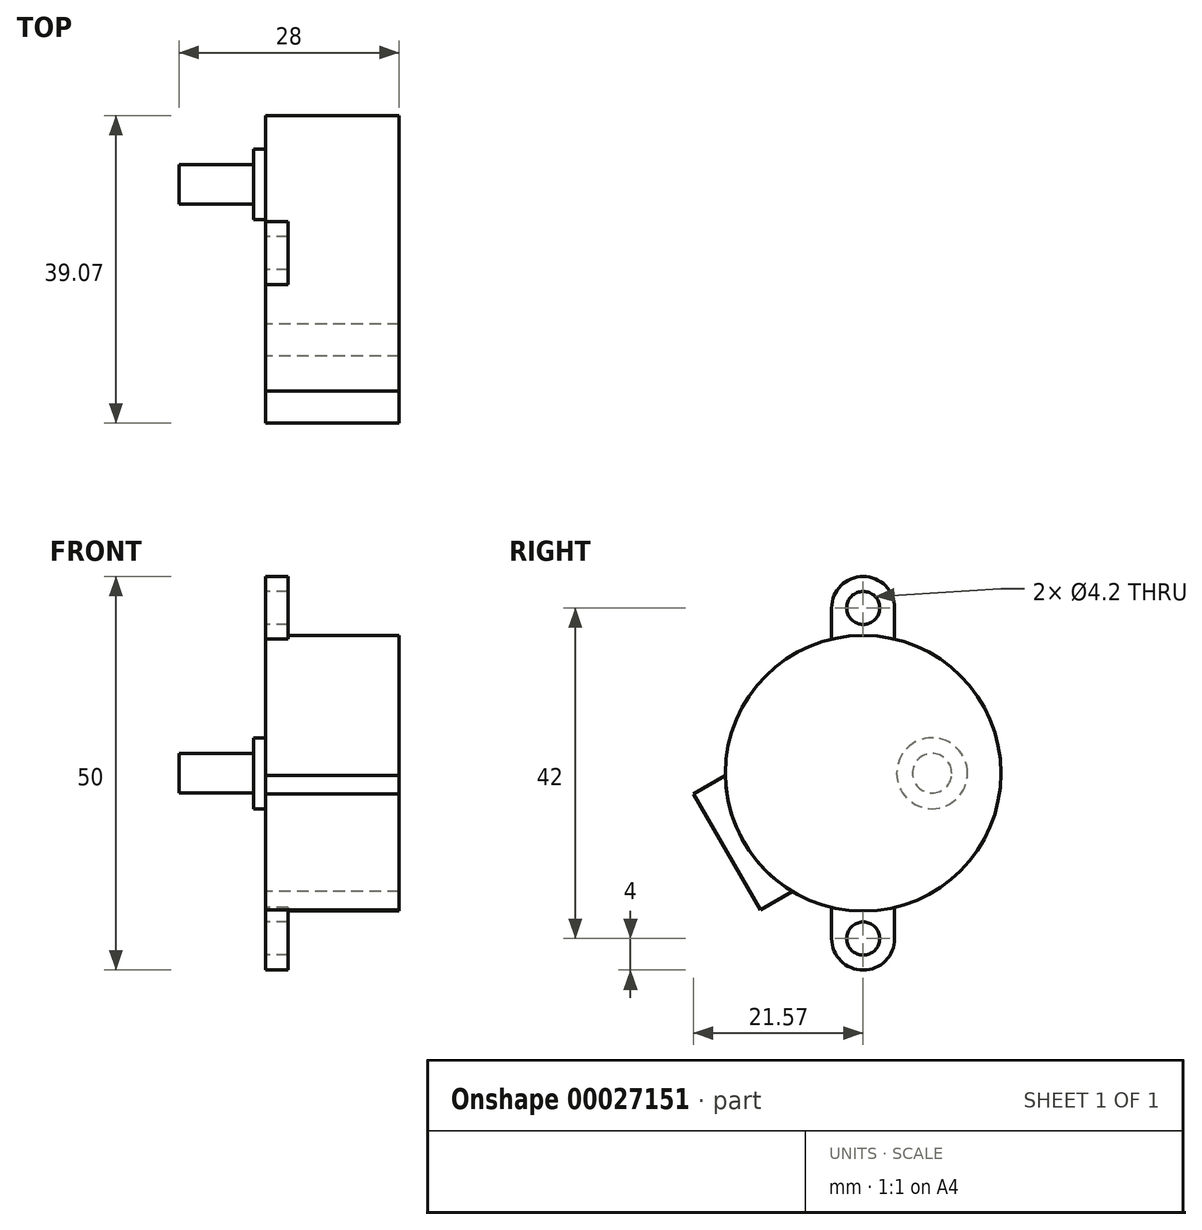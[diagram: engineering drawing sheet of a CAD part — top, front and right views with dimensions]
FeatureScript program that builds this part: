
annotation { "Feature Type Name" : "Feature", "Feature Type Description" : "" }
export const myFeature = defineFeature(function(context is Context, id is Id, definition is map)
    precondition{}
    {
        {
            var Q0;
            Q0=qCreatedBy(makeId("Top.planeOp"),FACE);
            var sketch = newSketch(context, id + "F0", { "sketchPlane" : qUnion([Q0])});
            skLineSegment(sketch, "E0", {"start": v(-25.01, 0) * mm, "end": v(67.35, 0) * mm, "construction": true});
            skLineSegment(sketch, "E1", {"start": v(17, 17.5) * mm, "end": v(17, -17.5) * mm});
            skLineSegment(sketch, "E2", {"start": v(17, -17.5) * mm, "end": v(0, -17.5) * mm});
            skLineSegment(sketch, "E3", {"start": v(0, -17.5) * mm, "end": v(0, 17.5) * mm});
            skLineSegment(sketch, "E4", {"start": v(0, 17.5) * mm, "end": v(17, 17.5) * mm});
            skPoint(sketch, "E5", {"position": v(0, 0) * mm});
            skLineSegment(sketch, "E6", {"start": v(-25.01, 8.75) * mm, "end": v(0, 8.75) * mm, "construction": true});
            skLineSegment(sketch, "E7", {"start": v(-11, 10.25) * mm, "end": v(-11, 7.25) * mm});
            skLineSegment(sketch, "E8", {"start": v(-11, 7.25) * mm, "end": v(-5, 7.25) * mm});
            skLineSegment(sketch, "E9", {"start": v(-5, 7.25) * mm, "end": v(-5, 6.25) * mm});
            skLineSegment(sketch, "E10", {"start": v(-11, 10.25) * mm, "end": v(-5, 10.25) * mm});
            skLineSegment(sketch, "E11", {"start": v(-5, 10.25) * mm, "end": v(-5, 11.25) * mm});
            skLineSegment(sketch, "E12", {"start": v(-5, 11.25) * mm, "end": v(-1.5, 11.25) * mm});
            skLineSegment(sketch, "E13", {"start": v(-1.5, 11.25) * mm, "end": v(-1.5, 13.25) * mm});
            skLineSegment(sketch, "E14", {"start": v(-1.5, 13.25) * mm, "end": v(0, 13.25) * mm});
            skLineSegment(sketch, "E15", {"start": v(-5, 6.25) * mm, "end": v(-1.5, 6.25) * mm});
            skLineSegment(sketch, "E16", {"start": v(-1.5, 6.25) * mm, "end": v(-1.5, 4.25) * mm});
            skLineSegment(sketch, "E17", {"start": v(-1.5, 4.25) * mm, "end": v(0, 4.25) * mm});
            skPoint(sketch, "E18", {"position": v(-11, 8.75) * mm});
            skLineSegment(sketch, "E19", {"start": v(-25.01, 17.5) * mm, "end": v(-25.01, 8.75) * mm, "construction": true});
            skLineSegment(sketch, "E20", {"start": v(-25.01, 8.75) * mm, "end": v(-25.01, 0) * mm, "construction": true});
            skLineSegment(sketch, "E21", {"start": v(-5, 11.25) * mm, "end": v(-11, 11.25) * mm});
            skLineSegment(sketch, "E22", {"start": v(-11, 11.25) * mm, "end": v(-11, 10.25) * mm});
            skLineSegment(sketch, "E23", {"start": v(-11, 7.25) * mm, "end": v(-11, 6.25) * mm});
            skLineSegment(sketch, "E24", {"start": v(-11, 6.25) * mm, "end": v(-5, 6.25) * mm});
            skLineSegment(sketch, "E25", {"start": v(-11, 8.75) * mm, "end": v(0, 8.75) * mm});
            skLineSegment(sketch, "E26", {"start": v(0, 0) * mm, "end": v(17, 0) * mm});
            skSolve(sketch);
        }
        {
            var Q0;
            Q0=makeQuery(id+"F0.imprint","IMPRINT",FACE,{"disambiguationData":[TD([[makeQuery(id+"F0.imprint","IMPRINT",EDGE,{"derivedFrom":sQuery(id+"F0.wireOp",EDGE,"E10")}),1.0]])]});
            var Q1;
            {var subQ2=sQuery(id+"F0.wireOp",EDGE,"E10");Q1=makeQuery(id+"F0.imprint","IMPRINT",FACE,{"disambiguationData":[TD([[makeQuery(id+"F0.imprint","IMPRINT",EDGE,{"derivedFrom":subQ2}),-1.0]])]});}
            var Q2;
            Q2=sQuery(id+"F0.wireOp",EDGE,"E25");
            revolve(context, id + "F1", {"entities" : qUnion([Q0, Q1]), "axis" : qUnion([Q2]), "revolveType" : RevolveType.FULL});
        }
        {
            var Q0;
            {var subQ1=sQuery(id+"F0.wireOp",EDGE,"E4");Q0=makeQuery(id+"F0.imprint","IMPRINT",FACE,{"disambiguationData":[TD([[makeQuery(id+"F0.imprint","IMPRINT",EDGE,{"derivedFrom":subQ1}),-1.0]])]});}
            var Q1;
            Q1=sQuery(id+"F0.wireOp",EDGE,"E26");
            revolve(context, id + "F2", {"entities" : qUnion([Q0]), "axis" : qUnion([Q1]), "revolveType" : RevolveType.FULL});
        }
        {
            var Q0;
            Q0=makeQuery(id+"F2.opRevolve","SWEPT_FACE",FACE,{"disambiguationData":[OSD([sQuery(id+"F0.wireOp",EDGE,"E3")])]});
            var sketch = newSketch(context, id + "F3", { "sketchPlane" : qUnion([Q0])});
            skCircle(sketch, "E27", {"center": v(0, 0) * mm, "radius": 17.5 * mm});
            skLineSegment(sketch, "E28", {"start": v(-17.5, 0) * mm, "end": v(17.5, 0) * mm, "construction": true});
            skLineSegment(sketch, "E29", {"start": v(4, 21) * mm, "end": v(4, -21) * mm});
            skLineSegment(sketch, "E30", {"start": v(4, -21) * mm, "end": v(-4, -21) * mm, "construction": true});
            skLineSegment(sketch, "E31", {"start": v(-4, -21) * mm, "end": v(-4, 21) * mm});
            skLineSegment(sketch, "E32", {"start": v(4, 21) * mm, "end": v(-4, 21) * mm, "construction": true});
            skPoint(sketch, "E33", {"position": v(0, 21) * mm});
            skPoint(sketch, "E34", {"position": v(0, -21) * mm});
            skLineSegment(sketch, "E35", {"start": v(0, 21) * mm, "end": v(0, -21) * mm, "construction": true});
            skCircle(sketch, "E36", {"center": v(0, 21) * mm, "radius": 2.1 * mm});
            skArc(sketch, "E37", {"start": v(4, 21) * mm, "mid": v(0, 25) * mm, "end": v(-4, 21) * mm});
            skArc(sketch, "E38", {"start": v(-4, -21) * mm, "mid": v(0, -25) * mm, "end": v(4, -21) * mm});
            skCircle(sketch, "E39", {"center": v(0, -21) * mm, "radius": 2.1 * mm});
            skLineSegment(sketch, "E40", {"start": v(-15.16, 8.75) * mm, "end": v(17.32, -10) * mm, "construction": true});
            skLineSegment(sketch, "E41", {"start": v(13.07, -17.36) * mm, "end": v(21.57, -2.64) * mm});
            skPoint(sketch, "E42", {"position": v(17.32, -10) * mm});
            skLineSegment(sketch, "E43", {"start": v(13.07, -17.36) * mm, "end": v(9, -15) * mm});
            skLineSegment(sketch, "E44", {"start": v(21.57, -2.64) * mm, "end": v(17.5, -0.29) * mm});
            skSolve(sketch);
        }
        {
            var Q0;
            Q0=makeQuery(id+"F3.imprint","IMPRINT",FACE,{"disambiguationData":[TD([[makeQuery(id+"F3.imprint","IMPRINT",EDGE,{"derivedFrom":sQuery(id+"F3.wireOp",EDGE,"E36")}),-1.0]])]});
            var Q1;
            {var subQ0=sQuery(id+"F3.wireOp",EDGE,"E38");Q1=makeQuery(id+"F3.imprint","IMPRINT",FACE,{"disambiguationData":[TD([[makeQuery(id+"F3.imprint","IMPRINT",EDGE,{"derivedFrom":subQ0}),1.0]])]});}
            extrude(context, id + "F4", {"entities" : qUnion([Q0, Q1]), "operationType" : NewBodyOperationType.ADD, "oppositeDirection" : true, "depth" : 2.9 * mm});
        }
        {
            var Q0;
            Q0=makeQuery(id+"F3.imprint","IMPRINT",FACE,{"disambiguationData":[TD([[makeQuery(id+"F3.imprint","IMPRINT",EDGE,{"derivedFrom":sQuery(id+"F3.wireOp",EDGE,"E41")}),1.0]])]});
            var Q1;
            Q1=makeQuery(id+"F2.opRevolve","SWEPT_FACE",FACE,{"disambiguationData":[OSD([sQuery(id+"F0.wireOp",EDGE,"E1")])]});
            extrude(context, id + "F5", {"entities" : qUnion([Q0]), "endBound" : BoundingType.UP_TO_SURFACE, "oppositeDirection" : true, "endBoundEntityFace" : qUnion([Q1]), "depth" : 25 * mm});
        }
    });
